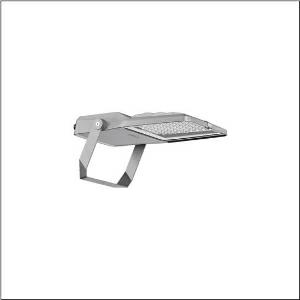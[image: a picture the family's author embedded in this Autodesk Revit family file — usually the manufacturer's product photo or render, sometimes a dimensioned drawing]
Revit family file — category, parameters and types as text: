
# Revit family: floodlight_fl_21_iq_mini___pl64_5xa7772b5e1a_cdb2
name_source: partatom
category: Lighting Fixtures
units: mm (PartAtom-declared; Revit-internal decimal feet)

## family parameters
Cut with Voids When Loaded = No
Host = Face
Light Source = No
Part Type = Normal
Room Calculation Point = No
Round Connector Dimension = Use Diameter
Shared = No

## types (1)
- --- (1 x LED, 5620 lm, 45.5 W, 4000K)
    Apparent Load = 46 VA
    CIE Flux Codes = 28 80 98 100 100
    Color Rendering = 80
    Color Temperature = 4000K
    Default Elevation = 1800 mm
    Description = Floodlight FL 21 iQ mini, floodlight, primary light control with lens, of PMMA, primary optical cover: protective disc, of toughened safety glass, transparent, light distribution: PL64, light emission: direct distribution, installation type: surface-mounted, LED, High Power LED, rated luminous flux: 5.620lm, luminous efficacy: 124lm/W, light colour: 840, colour temperature: 4000K, control gear: iQ Street-Remote/DALI, control: Street-Remote, Auto-Match, Temp-Guard, Night-Set, Smart-Wire, Desk-Remote (wireless, voltage-free reading and setting of iQ features in the workshop via application-optimized NFC function/RFID function), optimised constant luminous flux control (CLO 2.0), with terminal, 6-pole, mains connection: 220..240V, AC, 50/60Hz, start of lifetime: 46W, end of service life: 48W, reduction: 22W, luminaire housing, of diecast aluminium, powder-coated, Siteco® metallic grey (DB 702S), corrosivity category C5 mid according to DIN EN ISO 12944, suitable for swimming pools, chlorine-resistant, sealing non-destructively replaceable, mounting bracket, of steel, galvanised, powder-coated, Siteco® metallic grey (DB 702S), protection rating (complete): IP66, insulation class (complete): insulation class II (safety insulation), certification: CE, ENEC, VDE, protection symbol: D, impact resistance: IK08, permissible operating ambient temperature: -40..+40°C, permissible operating ambient temperature for outdoor applications: -40..+50°C, standard: DIN EN 12944, LABS conformity tested according to VDMA 24364:2018-05, packaging unit: 1 piece

Light Distribution: PL64
    Height = 70 mm
    Lamp = 1 x LED
    Lamp Light Flux = 5620 lm
    Lamp Power = 45.5 W
    Lamp count = 1
    Length = 485 mm
    Luminous efficacy = 124 lm/W
    Manufacturer = Siteco
    ModVariant = No
    Model = 5XA7772B5E1A
    Number of Poles = 1
    OnlyDefault = Yes
    Power Factor = 1
    Product Name = Floodlight FL 21 iQ mini | PL64
    Product group = floodlight | pylon annexe
    ProductGroupID = 6201
    Protection Class = Protection class II
    Protection Degree = IP 66
    RLX_Detail_Level = 1
    RLX_Emergency_Light_Flux = 0 lm
    RLX_Emergency_Type = 0
    RLX_Emergency_Type_DB = No
    RlxData = <blob elided: 96397 chars, md5=9381ebd3>
    Socket = socket
    Standby Power = 0 W
    System Light Flux = 5620 lm
    System Power = 46 W
    Type Comments = factory setting: luminous flux: 100 % | dim-lin: 254 | 463 mA
    Type Image = l_1006845.jpg
    URL = http://relux.com
    VarID = @adj_188187
    Voltage = 0 V
    Weight = 0.00 kg
    Width = 337 mm

## geometry (parser evidence)
native form markers: Blend x4, Sweep x13
no freeform markers — native parametric forms only
